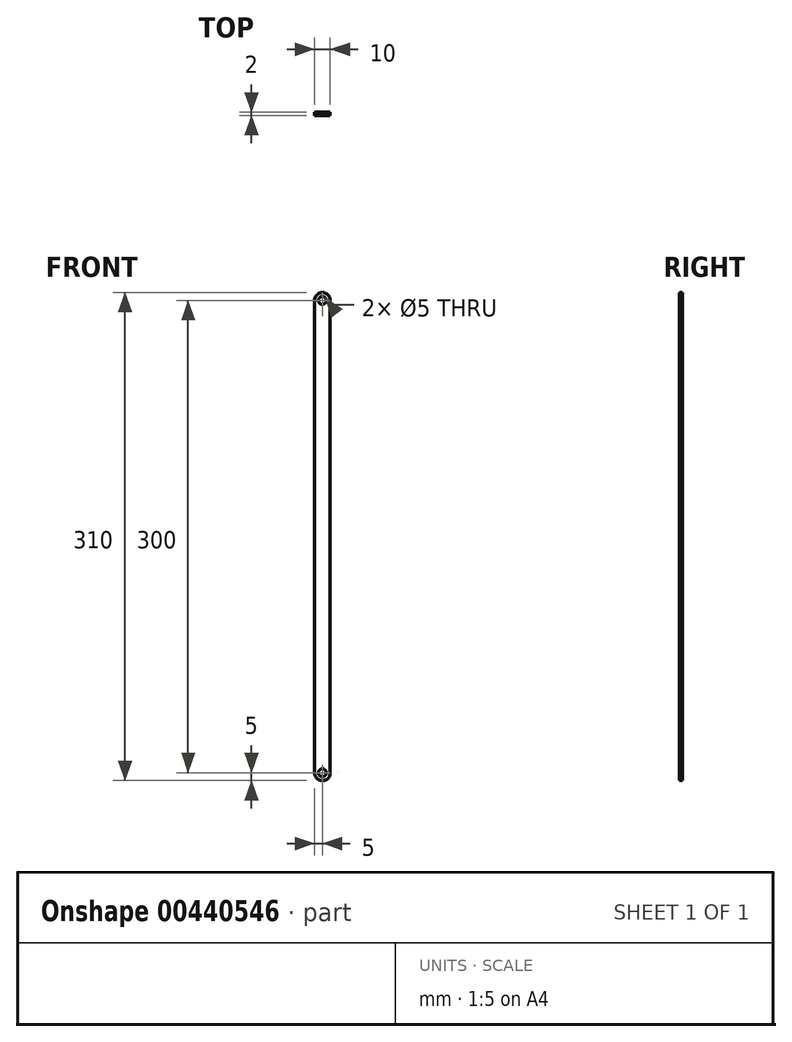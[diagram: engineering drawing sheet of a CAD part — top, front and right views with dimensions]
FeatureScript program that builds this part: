
annotation { "Feature Type Name" : "Feature", "Feature Type Description" : "" }
export const myFeature = defineFeature(function(context is Context, id is Id, definition is map)
    precondition{}
    {
        {
            var Q0;
            Q0=qCreatedBy(makeId("Front.planeOp"),FACE);
            var sketch = newSketch(context, id + "F0", { "sketchPlane" : qUnion([Q0])});
            skLineSegment(sketch, "E0.bottom", {"start": v(0, 160) * mm, "end": v(0, 160) * mm});
            skLineSegment(sketch, "E0.top", {"start": v(0, -150) * mm, "end": v(0, -150) * mm});
            skLineSegment(sketch, "E0.left", {"start": v(-5, 155) * mm, "end": v(-5, -145) * mm});
            skLineSegment(sketch, "E0.right", {"start": v(5, 155) * mm, "end": v(5, -145) * mm});
            skPoint(sketch, "E0.middle", {"position": v(0, 0) * mm});
            skArc(sketch, "E1.filletArc", {"start": v(0, 160) * mm, "mid": v(-3.54, 158.54) * mm, "end": v(-5, 155) * mm});
            skArc(sketch, "E2.filletArc", {"start": v(5, 155) * mm, "mid": v(3.54, 158.54) * mm, "end": v(0, 160) * mm});
            skArc(sketch, "E3.filletArc", {"start": v(-5, -145) * mm, "mid": v(-3.54, -148.54) * mm, "end": v(0, -150) * mm});
            skArc(sketch, "E4.filletArc", {"start": v(0, -150) * mm, "mid": v(3.54, -148.54) * mm, "end": v(5, -145) * mm});
            skSolve(sketch);
        }
        {
            var Q0;
            Q0=makeQuery(id+"F0.imprint","IMPRINT",FACE,{"disambiguationData":[TD([[makeQuery(id+"F0.imprint","IMPRINT",EDGE,{"derivedFrom":sQuery(id+"F0.wireOp",EDGE,"E0.left")}),1.0]])]});
            extrude(context, id + "F1", {"entities" : qUnion([Q0]), "depth" : 2 * mm});
        }
        {
            var Q0;
            Q0=sQuery(id+"F0.wireOp",VERTEX,"E1.filletArc.center");
            var Q1;
            Q1=makeQuery(id+"F1.opExtrude","SWEPT_BODY",BODY,{"disambiguationData":[OSD([sQuery(id+"F0.wireOp",EDGE,"E0.left"),sQuery(id+"F0.wireOp",EDGE,"E0.right"),sQuery(id+"F0.wireOp",EDGE,"E1.filletArc"),sQuery(id+"F0.wireOp",EDGE,"E2.filletArc"),sQuery(id+"F0.wireOp",EDGE,"E3.filletArc"),sQuery(id+"F0.wireOp",EDGE,"E4.filletArc")])]});
            hole(context, id + "F2", {"style" : HoleStyle.SIMPLE, "endStyle" : HoleEndStyle.THROUGH, "oppositeDirection" : true, "holeDiameter" : 5 * mm, "isTappedThrough" : true, "tappedDepth" : 12 * mm, "tapClearance" : 3, "startFromSketch" : true, "locations" : qUnion([Q0]), "scope" : qUnion([Q1])});
        }
        {
            var Q0;
            Q0=sQuery(id+"F0.wireOp",VERTEX,"E3.filletArc.center");
            var Q1;
            Q1=makeQuery(id+"F1.opExtrude","SWEPT_BODY",BODY,{"disambiguationData":[OSD([sQuery(id+"F0.wireOp",EDGE,"E0.left"),sQuery(id+"F0.wireOp",EDGE,"E0.right"),sQuery(id+"F0.wireOp",EDGE,"E1.filletArc"),sQuery(id+"F0.wireOp",EDGE,"E2.filletArc"),sQuery(id+"F0.wireOp",EDGE,"E3.filletArc"),sQuery(id+"F0.wireOp",EDGE,"E4.filletArc")])]});
            hole(context, id + "F3", {"style" : HoleStyle.SIMPLE, "endStyle" : HoleEndStyle.THROUGH, "oppositeDirection" : true, "holeDiameter" : 5 * mm, "isTappedThrough" : true, "tappedDepth" : 12 * mm, "tapClearance" : 3, "startFromSketch" : true, "locations" : qUnion([Q0]), "scope" : qUnion([Q1])});
        }
    });
